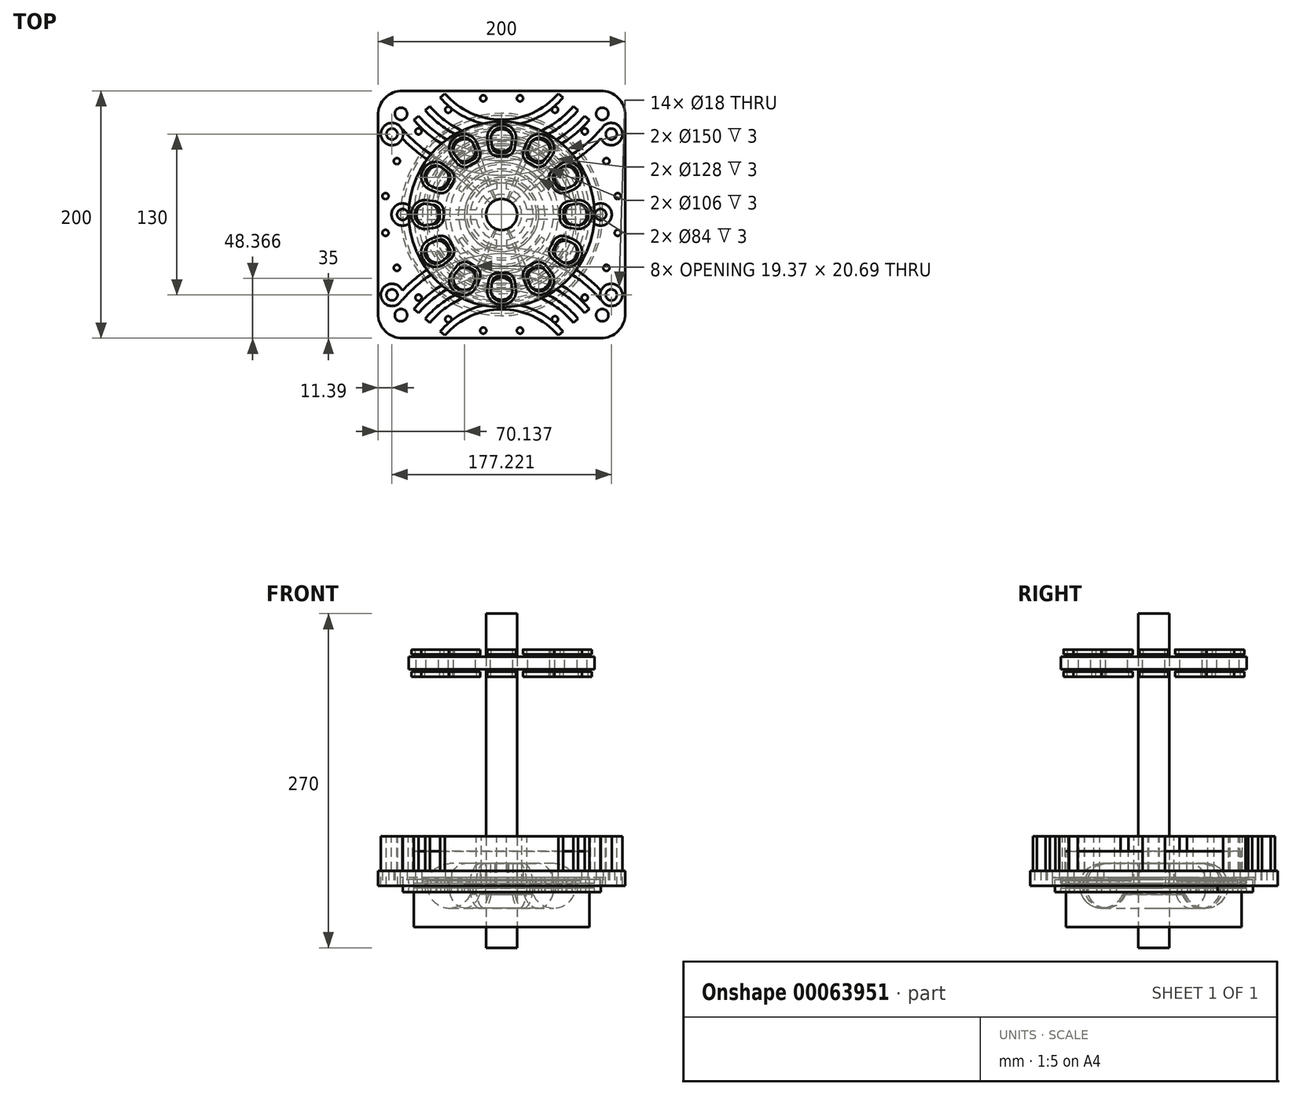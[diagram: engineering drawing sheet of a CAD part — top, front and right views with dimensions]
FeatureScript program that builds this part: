
annotation { "Feature Type Name" : "Feature", "Feature Type Description" : "" }
export const myFeature = defineFeature(function(context is Context, id is Id, definition is map)
    precondition{}
    {
        {
            var Q0;
            Q0=qCreatedBy(makeId("Top.planeOp"),FACE);
            var sketch = newSketch(context, id + "F0", { "sketchPlane" : qUnion([Q0])});
            skCircle(sketch, "E0", {"center": v(0, 0) * mm, "radius": 80 * mm});
            skCircle(sketch, "E1", {"center": v(0, 0) * mm, "radius": 30 * mm});
            skLineSegment(sketch, "E2", {"start": v(0, 30) * mm, "end": v(0, 80) * mm});
            skCircle(sketch, "E3", {"center": v(0, 0) * mm, "radius": 12.5 * mm});
            skLineSegment(sketch, "E4", {"start": v(0, 30) * mm, "end": v(0, 12.5) * mm});
            skLineSegment(sketch, "E5", {"start": v(-61.28, 51.42) * mm, "end": v(-22.98, 19.28) * mm});
            skLineSegment(sketch, "E6", {"start": v(0, 80) * mm, "end": v(0, 109.43) * mm, "construction": true});
            skLineSegment(sketch, "E7.MirrorCS", {"start": v(61.28, 51.42) * mm, "end": v(22.98, 19.28) * mm});
            skLineSegment(sketch, "E8", {"start": v(80, 0) * mm, "end": v(100, 0) * mm});
            skLineSegment(sketch, "E9", {"start": v(100, 0) * mm, "end": v(100, 80) * mm});
            skLineSegment(sketch, "E10", {"start": v(80, 100) * mm, "end": v(0, 100) * mm});
            skLineSegment(sketch, "E11", {"start": v(0, 100) * mm, "end": v(0, 80) * mm});
            skCircle(sketch, "E12", {"center": v(0, 0) * mm, "radius": 90 * mm});
            skLineSegment(sketch, "E13", {"start": v(0, 0) * mm, "end": v(0, -92.84) * mm, "construction": true});
            skLineSegment(sketch, "E14", {"start": v(0, 0) * mm, "end": v(-115.3, 0) * mm, "construction": true});
            skPoint(sketch, "E15", {"position": v(0, 90) * mm});
            skCircle(sketch, "E16", {"center": v(0, 0) * mm, "radius": 95 * mm, "construction": true});
            skCircle(sketch, "E17", {"center": v(67.18, 67.18) * mm, "radius": 2.5 * mm});
            skCircle(sketch, "E18", {"center": v(84.65, 43.13) * mm, "radius": 2.5 * mm});
            skCircle(sketch, "E19", {"center": v(93.83, 14.86) * mm, "radius": 2.5 * mm});
            skCircle(sketch, "E20", {"center": v(43.13, 84.65) * mm, "radius": 2.5 * mm});
            skCircle(sketch, "E21", {"center": v(14.86, 93.83) * mm, "radius": 2.5 * mm});
            skLineSegment(sketch, "E22", {"start": v(0, 0) * mm, "end": v(67.18, 67.18) * mm, "construction": true});
            skLineSegment(sketch, "E23", {"start": v(43.13, 84.65) * mm, "end": v(0, 0) * mm, "construction": true});
            skLineSegment(sketch, "E24", {"start": v(14.86, 93.83) * mm, "end": v(0, 0) * mm, "construction": true});
            skLineSegment(sketch, "E25", {"start": v(84.65, 43.13) * mm, "end": v(0, 0) * mm, "construction": true});
            skLineSegment(sketch, "E26", {"start": v(93.83, 14.86) * mm, "end": v(0, 0) * mm, "construction": true});
            skCircle(sketch, "E27", {"center": v(81.32, 81.32) * mm, "radius": 5 * mm});
            skLineSegment(sketch, "E28", {"start": v(67.18, 67.18) * mm, "end": v(81.32, 81.32) * mm, "construction": true});
            skCircle(sketch, "E29", {"center": v(0, 0) * mm, "radius": 115 * mm, "construction": true});
            skPoint(sketch, "E30.visualSharp", {"position": v(100, 100) * mm});
            skArc(sketch, "E30.filletArc", {"start": v(100, 80) * mm, "mid": v(94.14, 94.14) * mm, "end": v(80, 100) * mm});
            skSolve(sketch);
        }
        {
            var Q0;
            Q0=qCreatedBy(makeId("Right.planeOp"),FACE);
            var sketch = newSketch(context, id + "F1", { "sketchPlane" : qUnion([Q0])});
            skLineSegment(sketch, "E31.rect.bottom", {"start": v(80, -5) * mm, "end": v(75, -5) * mm});
            skLineSegment(sketch, "E31.rect.top", {"start": v(80, 5) * mm, "end": v(75, 5) * mm});
            skLineSegment(sketch, "E31.rect.left", {"start": v(80, -5) * mm, "end": v(80, 5) * mm});
            skLineSegment(sketch, "E31.rect.right", {"start": v(30, -5) * mm, "end": v(30, 5) * mm});
            skPoint(sketch, "E31.rect.middle", {"position": v(55, 0) * mm});
            skLineSegment(sketch, "E32.rect.bottom", {"start": v(30, -2) * mm, "end": v(12.5, -2) * mm});
            skLineSegment(sketch, "E32.rect.top", {"start": v(30, 2) * mm, "end": v(12.5, 2) * mm});
            skLineSegment(sketch, "E32.rect.left", {"start": v(30, -2) * mm, "end": v(30, 2) * mm});
            skLineSegment(sketch, "E32.rect.right", {"start": v(12.5, -2) * mm, "end": v(12.5, 2) * mm});
            skPoint(sketch, "E32.rect.middle", {"position": v(21.25, 0) * mm});
            skLineSegment(sketch, "E33", {"start": v(0, -7.1) * mm, "end": v(0, -52.53) * mm});
            skLineSegment(sketch, "E34", {"start": v(35, 5) * mm, "end": v(35, 2) * mm});
            skLineSegment(sketch, "E35", {"start": v(35, 2) * mm, "end": v(42, 2) * mm});
            skLineSegment(sketch, "E36", {"start": v(42, 2) * mm, "end": v(42, 5) * mm});
            skLineSegment(sketch, "E37.top", {"start": v(46, 2) * mm, "end": v(53, 2) * mm});
            skLineSegment(sketch, "E37.left", {"start": v(46, 5) * mm, "end": v(46, 2) * mm});
            skLineSegment(sketch, "E37.right", {"start": v(53, 5) * mm, "end": v(53, 2) * mm});
            skLineSegment(sketch, "E38.top", {"start": v(57, 2) * mm, "end": v(64, 2) * mm});
            skLineSegment(sketch, "E38.left", {"start": v(57, 5) * mm, "end": v(57, 2) * mm});
            skLineSegment(sketch, "E38.right", {"start": v(64, 5) * mm, "end": v(64, 2) * mm});
            skLineSegment(sketch, "E39.top", {"start": v(68, 2) * mm, "end": v(75, 2) * mm});
            skLineSegment(sketch, "E39.left", {"start": v(68, 5) * mm, "end": v(68, 2) * mm});
            skLineSegment(sketch, "E39.right", {"start": v(75, 5) * mm, "end": v(75, 2) * mm});
            skPoint(sketch, "E40", {"position": v(38.5, 2) * mm});
            skPoint(sketch, "E41", {"position": v(49.5, 2) * mm});
            skPoint(sketch, "E42", {"position": v(60.5, 2) * mm});
            skPoint(sketch, "E43", {"position": v(71.5, 2) * mm});
            skLineSegment(sketch, "E44.MirrorCS", {"start": v(75, -5) * mm, "end": v(75, -2) * mm});
            skLineSegment(sketch, "E45.MirrorCS", {"start": v(68, -2) * mm, "end": v(75, -2) * mm});
            skLineSegment(sketch, "E46.MirrorCS", {"start": v(68, -5) * mm, "end": v(68, -2) * mm});
            skLineSegment(sketch, "E47.MirrorCS", {"start": v(64, -5) * mm, "end": v(64, -2) * mm});
            skLineSegment(sketch, "E48.MirrorCS", {"start": v(57, -2) * mm, "end": v(64, -2) * mm});
            skLineSegment(sketch, "E49.MirrorCS", {"start": v(57, -5) * mm, "end": v(57, -2) * mm});
            skLineSegment(sketch, "E50.MirrorCS", {"start": v(53, -5) * mm, "end": v(53, -2) * mm});
            skLineSegment(sketch, "E51.MirrorCS", {"start": v(46, -2) * mm, "end": v(53, -2) * mm});
            skLineSegment(sketch, "E52.MirrorCS", {"start": v(46, -5) * mm, "end": v(46, -2) * mm});
            skLineSegment(sketch, "E53.MirrorCS", {"start": v(42, -2) * mm, "end": v(42, -5) * mm});
            skLineSegment(sketch, "E54.MirrorCS", {"start": v(35, -2) * mm, "end": v(42, -2) * mm});
            skLineSegment(sketch, "E55.MirrorCS", {"start": v(35, -5) * mm, "end": v(35, -2) * mm});
            skLineSegment(sketch, "E56.trimOffspring", {"start": v(35, 5) * mm, "end": v(30, 5) * mm});
            skLineSegment(sketch, "E57.trimOffspring", {"start": v(46, 5) * mm, "end": v(42, 5) * mm});
            skLineSegment(sketch, "E58.trimOffspring", {"start": v(57, 5) * mm, "end": v(53, 5) * mm});
            skLineSegment(sketch, "E59.trimOffspring", {"start": v(68, 5) * mm, "end": v(64, 5) * mm});
            skLineSegment(sketch, "E60.trimOffspring", {"start": v(68, -5) * mm, "end": v(64, -5) * mm});
            skLineSegment(sketch, "E61.trimOffspring", {"start": v(57, -5) * mm, "end": v(53, -5) * mm});
            skLineSegment(sketch, "E62.trimOffspring", {"start": v(46, -5) * mm, "end": v(42, -5) * mm});
            skLineSegment(sketch, "E63.trimOffspring", {"start": v(35, -5) * mm, "end": v(30, -5) * mm});
            skLineSegment(sketch, "E64.0", {"start": v(36.75, 6.75) * mm, "end": v(28.25, 6.75) * mm});
            skLineSegment(sketch, "E64.1", {"start": v(28.25, -6.75) * mm, "end": v(28.25, 6.75) * mm});
            skLineSegment(sketch, "E64.2", {"start": v(36.75, -6.75) * mm, "end": v(28.25, -6.75) * mm});
            skLineSegment(sketch, "E64.3", {"start": v(36.75, -6.75) * mm, "end": v(36.75, -3.75) * mm});
            skLineSegment(sketch, "E64.4", {"start": v(36.75, -3.75) * mm, "end": v(40.25, -3.75) * mm});
            skLineSegment(sketch, "E64.5", {"start": v(40.25, -3.75) * mm, "end": v(40.25, -6.75) * mm});
            skLineSegment(sketch, "E64.6", {"start": v(47.75, -6.75) * mm, "end": v(40.25, -6.75) * mm});
            skLineSegment(sketch, "E64.7", {"start": v(47.75, -6.75) * mm, "end": v(47.75, -3.75) * mm});
            skLineSegment(sketch, "E64.8", {"start": v(47.75, -3.75) * mm, "end": v(51.25, -3.75) * mm});
            skLineSegment(sketch, "E64.9", {"start": v(51.25, -6.75) * mm, "end": v(51.25, -3.75) * mm});
            skLineSegment(sketch, "E64.10", {"start": v(58.75, -6.75) * mm, "end": v(51.25, -6.75) * mm});
            skLineSegment(sketch, "E64.11", {"start": v(36.75, 6.75) * mm, "end": v(36.75, 3.75) * mm});
            skLineSegment(sketch, "E64.12", {"start": v(58.75, -6.75) * mm, "end": v(58.75, -3.75) * mm});
            skLineSegment(sketch, "E64.13", {"start": v(58.75, -3.75) * mm, "end": v(62.25, -3.75) * mm});
            skLineSegment(sketch, "E64.14", {"start": v(62.25, 6.75) * mm, "end": v(62.25, 3.75) * mm});
            skLineSegment(sketch, "E64.15", {"start": v(58.75, 3.75) * mm, "end": v(62.25, 3.75) * mm});
            skLineSegment(sketch, "E64.16", {"start": v(58.75, 6.75) * mm, "end": v(58.75, 3.75) * mm});
            skLineSegment(sketch, "E64.17", {"start": v(58.75, 6.75) * mm, "end": v(51.25, 6.75) * mm});
            skLineSegment(sketch, "E64.18", {"start": v(51.25, 6.75) * mm, "end": v(51.25, 3.75) * mm});
            skLineSegment(sketch, "E64.19", {"start": v(47.75, 3.75) * mm, "end": v(51.25, 3.75) * mm});
            skLineSegment(sketch, "E64.20", {"start": v(36.75, 3.75) * mm, "end": v(40.25, 3.75) * mm});
            skLineSegment(sketch, "E64.21", {"start": v(40.25, 3.75) * mm, "end": v(40.25, 6.75) * mm});
            skLineSegment(sketch, "E64.22", {"start": v(47.75, 6.75) * mm, "end": v(40.25, 6.75) * mm});
            skLineSegment(sketch, "E64.23", {"start": v(47.75, 6.75) * mm, "end": v(47.75, 3.75) * mm});
            skLineSegment(sketch, "E64.24", {"start": v(69.75, 6.75) * mm, "end": v(62.25, 6.75) * mm});
            skLineSegment(sketch, "E64.25", {"start": v(69.75, 6.75) * mm, "end": v(69.75, 3.75) * mm});
            skLineSegment(sketch, "E64.26", {"start": v(69.75, 3.75) * mm, "end": v(73.25, 3.75) * mm});
            skLineSegment(sketch, "E64.27", {"start": v(73.25, 6.75) * mm, "end": v(73.25, 3.75) * mm});
            skLineSegment(sketch, "E64.28", {"start": v(81.75, 6.75) * mm, "end": v(73.25, 6.75) * mm});
            skLineSegment(sketch, "E64.29", {"start": v(81.75, -6.75) * mm, "end": v(81.75, 6.75) * mm});
            skLineSegment(sketch, "E64.30", {"start": v(81.75, -6.75) * mm, "end": v(73.25, -6.75) * mm});
            skLineSegment(sketch, "E64.31", {"start": v(73.25, -6.75) * mm, "end": v(73.25, -3.75) * mm});
            skLineSegment(sketch, "E64.32", {"start": v(69.75, -3.75) * mm, "end": v(73.25, -3.75) * mm});
            skLineSegment(sketch, "E64.33", {"start": v(69.75, -6.75) * mm, "end": v(69.75, -3.75) * mm});
            skLineSegment(sketch, "E64.34", {"start": v(69.75, -6.75) * mm, "end": v(62.25, -6.75) * mm});
            skLineSegment(sketch, "E64.35", {"start": v(62.25, -6.75) * mm, "end": v(62.25, -3.75) * mm});
            skLineSegment(sketch, "E65.bottom", {"start": v(90, 0) * mm, "end": v(16.2, 0) * mm});
            skLineSegment(sketch, "E65.top", {"start": v(90, 12) * mm, "end": v(16.2, 12) * mm});
            skLineSegment(sketch, "E65.left", {"start": v(90, 0) * mm, "end": v(90, 12) * mm});
            skLineSegment(sketch, "E65.right", {"start": v(16.2, 0) * mm, "end": v(16.2, 12) * mm});
            skLineSegment(sketch, "E66.MirrorCS", {"start": v(90, 0) * mm, "end": v(90, -12) * mm});
            skLineSegment(sketch, "E67.MirrorCS", {"start": v(90, -12) * mm, "end": v(16.2, -12) * mm});
            skLineSegment(sketch, "E68.MirrorCS", {"start": v(16.2, 0) * mm, "end": v(16.2, -12) * mm});
            skSolve(sketch);
        }
        {
            var Q0;
            {var subQ0=sQuery(id+"F1.wireOp",EDGE,"E31.rect.top");Q0=makeQuery(id+"F1.imprint","IMPRINT",FACE,{"disambiguationData":[TD([[makeQuery(id+"F1.imprint","IMPRINT",EDGE,{"derivedFrom":subQ0}),1.0]])]});}
            var Q1;
            {var subQ1=sQuery(id+"F1.wireOp",EDGE,"E31.rect.bottom");Q1=makeQuery(id+"F1.imprint","IMPRINT",FACE,{"disambiguationData":[TD([[makeQuery(id+"F1.imprint","IMPRINT",EDGE,{"derivedFrom":subQ1}),-1.0]])]});}
            var Q2;
            Q2=sQuery(id+"F1.wireOp",EDGE,"E33");
            revolve(context, id + "F2", {"entities" : qUnion([Q0, Q1]), "axis" : qUnion([Q2]), "revolveType" : RevolveType.SYMMETRIC, "angle" : 100 * degree});
        }
        {
            var Q0;
            {var subQ5=sQuery(id+"F1.wireOp",EDGE,"E32.rect.right");Q0=makeQuery(id+"F1.imprint","IMPRINT",FACE,{"disambiguationData":[TD([[makeQuery(id+"F1.imprint","IMPRINT",EDGE,{"derivedFrom":subQ5}),-1.0]])]});}
            var Q1;
            {var subQ0=sQuery(id+"F1.wireOp",EDGE,"E65.right");var subQ1=sQuery(id+"F1.wireOp",EDGE,"E32.rect.top");var subQ2=makeQuery(id+"F1.imprint","INTERSECT",VERTEX,{"derivedFrom":[subQ1,subQ0]});Q1=makeQuery(id+"F1.imprint","IMPRINT",FACE,{"disambiguationData":[TD([[makeQuery(id+"F1.imprint","IMPRINT",EDGE,{"disambiguationData":[TD([[subQ2,1.0]])],"derivedFrom":subQ1}),1.0]])]});}
            var Q2;
            {var subQ1=sQuery(id+"F1.wireOp",EDGE,"E32.rect.top");var subQ3=sQuery(id+"F1.wireOp",EDGE,"E64.1");var subQ4=makeQuery(id+"F1.imprint","INTERSECT",VERTEX,{"derivedFrom":[subQ1,subQ3]});Q2=makeQuery(id+"F1.imprint","IMPRINT",FACE,{"disambiguationData":[TD([[makeQuery(id+"F1.imprint","IMPRINT",EDGE,{"disambiguationData":[TD([[subQ4,1.0]])],"derivedFrom":subQ3}),-1.0]])]});}
            var Q3;
            {var subQ1=sQuery(id+"F1.wireOp",EDGE,"E32.rect.bottom");var subQ3=sQuery(id+"F1.wireOp",EDGE,"E64.1");var subQ4=makeQuery(id+"F1.imprint","INTERSECT",VERTEX,{"derivedFrom":[subQ1,subQ3]});Q3=makeQuery(id+"F1.imprint","IMPRINT",FACE,{"disambiguationData":[TD([[makeQuery(id+"F1.imprint","IMPRINT",EDGE,{"disambiguationData":[TD([[subQ4,-1.0]])],"derivedFrom":subQ3}),-1.0]])]});}
            var Q4;
            {var subQ0=sQuery(id+"F1.wireOp",EDGE,"E68.MirrorCS");var subQ1=sQuery(id+"F1.wireOp",EDGE,"E32.rect.bottom");var subQ2=makeQuery(id+"F1.imprint","INTERSECT",VERTEX,{"derivedFrom":[subQ1,subQ0]});Q4=makeQuery(id+"F1.imprint","IMPRINT",FACE,{"disambiguationData":[TD([[makeQuery(id+"F1.imprint","IMPRINT",EDGE,{"disambiguationData":[TD([[subQ2,1.0]])],"derivedFrom":subQ1}),-1.0]])]});}
            var Q5;
            Q5=makeQuery(id+"F2.opRevolve","SWEPT_FACE",FACE,{"disambiguationData":[OSD([sQuery(id+"F1.wireOp",EDGE,"E31.rect.left")])]});
            revolve(context, id + "F3", {"operationType" : NewBodyOperationType.ADD, "entities" : qUnion([Q0, Q1, Q2, Q3, Q4]), "axis" : qUnion([Q5]), "revolveType" : RevolveType.FULL});
        }
        {
            var Q0;
            {var subQ7=sQuery(id+"F1.wireOp",EDGE,"E64.0");Q0=makeQuery(id+"F1.imprint","IMPRINT",FACE,{"disambiguationData":[TD([[makeQuery(id+"F1.imprint","IMPRINT",EDGE,{"derivedFrom":subQ7}),-1.0]])]});}
            var Q1;
            Q1=sQuery(id+"F1.wireOp",EDGE,"E33");
            revolve(context, id + "F4", {"entities" : qUnion([Q0]), "axis" : qUnion([Q1]), "revolveType" : RevolveType.FULL});
        }
        {
            var Q0;
            {var subQ5=sQuery(id+"F0.wireOp",EDGE,"E9");Q0=makeQuery(id+"F0.imprint","IMPRINT",FACE,{"disambiguationData":[TD([[makeQuery(id+"F0.imprint","IMPRINT",EDGE,{"derivedFrom":subQ5}),1.0]])]});}
            extrude(context, id + "F5", {"entities" : qUnion([Q0]), "depth" : 12 * mm});
        }
        {
            var Q0;
            Q0=makeQuery(id+"F5.opExtrude","SWEPT_BODY",BODY,{"disambiguationData":[OSD([sQuery(id+"F0.wireOp",EDGE,"E8"),sQuery(id+"F0.wireOp",EDGE,"E9"),sQuery(id+"F0.wireOp",EDGE,"E10"),sQuery(id+"F0.wireOp",EDGE,"E11"),sQuery(id+"F0.wireOp",EDGE,"E12"),sQuery(id+"F0.wireOp",EDGE,"E17"),sQuery(id+"F0.wireOp",EDGE,"E18"),sQuery(id+"F0.wireOp",EDGE,"E19"),sQuery(id+"F0.wireOp",EDGE,"E20"),sQuery(id+"F0.wireOp",EDGE,"E21"),sQuery(id+"F0.wireOp",EDGE,"E27"),sQuery(id+"F0.wireOp",EDGE,"E30.filletArc")])]});
            var Q1;
            Q1=qCreatedBy(makeId("Front.planeOp"),FACE);
            mirror(context, id + "F6", {"entities" : qUnion([Q0]), "mirrorPlane" : qUnion([Q1])});
        }
        {
            var Q0;
            Q0=makeQuery(id+"F5.opExtrude","SWEPT_BODY",BODY,{"disambiguationData":[OSD([sQuery(id+"F0.wireOp",EDGE,"E8"),sQuery(id+"F0.wireOp",EDGE,"E9"),sQuery(id+"F0.wireOp",EDGE,"E10"),sQuery(id+"F0.wireOp",EDGE,"E11"),sQuery(id+"F0.wireOp",EDGE,"E12"),sQuery(id+"F0.wireOp",EDGE,"E17"),sQuery(id+"F0.wireOp",EDGE,"E18"),sQuery(id+"F0.wireOp",EDGE,"E19"),sQuery(id+"F0.wireOp",EDGE,"E20"),sQuery(id+"F0.wireOp",EDGE,"E21"),sQuery(id+"F0.wireOp",EDGE,"E27"),sQuery(id+"F0.wireOp",EDGE,"E30.filletArc")])]});
            var Q1;
            Q1=makeQuery(id+"F6.opPattern","COPY",BODY,{"derivedFrom":makeQuery(id+"F5.opExtrude","SWEPT_BODY",BODY,{"disambiguationData":[OSD([sQuery(id+"F0.wireOp",EDGE,"E8"),sQuery(id+"F0.wireOp",EDGE,"E9"),sQuery(id+"F0.wireOp",EDGE,"E10"),sQuery(id+"F0.wireOp",EDGE,"E11"),sQuery(id+"F0.wireOp",EDGE,"E12"),sQuery(id+"F0.wireOp",EDGE,"E17"),sQuery(id+"F0.wireOp",EDGE,"E18"),sQuery(id+"F0.wireOp",EDGE,"E19"),sQuery(id+"F0.wireOp",EDGE,"E20"),sQuery(id+"F0.wireOp",EDGE,"E21"),sQuery(id+"F0.wireOp",EDGE,"E27"),sQuery(id+"F0.wireOp",EDGE,"E30.filletArc")])]}),"instanceName":"1"});
            var Q2;
            Q2=qCreatedBy(makeId("Right.planeOp"),FACE);
            mirror(context, id + "F7", {"entities" : qUnion([Q0, Q1]), "mirrorPlane" : qUnion([Q2])});
        }
        {
            var Q0;
            Q0=makeQuery(id+"F5.opExtrude","SWEPT_BODY",BODY,{"disambiguationData":[OSD([sQuery(id+"F0.wireOp",EDGE,"E8"),sQuery(id+"F0.wireOp",EDGE,"E9"),sQuery(id+"F0.wireOp",EDGE,"E10"),sQuery(id+"F0.wireOp",EDGE,"E11"),sQuery(id+"F0.wireOp",EDGE,"E12"),sQuery(id+"F0.wireOp",EDGE,"E17"),sQuery(id+"F0.wireOp",EDGE,"E18"),sQuery(id+"F0.wireOp",EDGE,"E19"),sQuery(id+"F0.wireOp",EDGE,"E20"),sQuery(id+"F0.wireOp",EDGE,"E21"),sQuery(id+"F0.wireOp",EDGE,"E27"),sQuery(id+"F0.wireOp",EDGE,"E30.filletArc")])]});
            var Q1;
            Q1=makeQuery(id+"F7.opPattern","COPY",BODY,{"derivedFrom":makeQuery(id+"F5.opExtrude","SWEPT_BODY",BODY,{"disambiguationData":[OSD([sQuery(id+"F0.wireOp",EDGE,"E8"),sQuery(id+"F0.wireOp",EDGE,"E9"),sQuery(id+"F0.wireOp",EDGE,"E10"),sQuery(id+"F0.wireOp",EDGE,"E11"),sQuery(id+"F0.wireOp",EDGE,"E12"),sQuery(id+"F0.wireOp",EDGE,"E17"),sQuery(id+"F0.wireOp",EDGE,"E18"),sQuery(id+"F0.wireOp",EDGE,"E19"),sQuery(id+"F0.wireOp",EDGE,"E20"),sQuery(id+"F0.wireOp",EDGE,"E21"),sQuery(id+"F0.wireOp",EDGE,"E27"),sQuery(id+"F0.wireOp",EDGE,"E30.filletArc")])]}),"instanceName":"1"});
            var Q2;
            Q2=makeQuery(id+"F7.opPattern","COPY",BODY,{"derivedFrom":makeQuery(id+"F6.opPattern","COPY",BODY,{"derivedFrom":makeQuery(id+"F5.opExtrude","SWEPT_BODY",BODY,{"disambiguationData":[OSD([sQuery(id+"F0.wireOp",EDGE,"E8"),sQuery(id+"F0.wireOp",EDGE,"E9"),sQuery(id+"F0.wireOp",EDGE,"E10"),sQuery(id+"F0.wireOp",EDGE,"E11"),sQuery(id+"F0.wireOp",EDGE,"E12"),sQuery(id+"F0.wireOp",EDGE,"E17"),sQuery(id+"F0.wireOp",EDGE,"E18"),sQuery(id+"F0.wireOp",EDGE,"E19"),sQuery(id+"F0.wireOp",EDGE,"E20"),sQuery(id+"F0.wireOp",EDGE,"E21"),sQuery(id+"F0.wireOp",EDGE,"E27"),sQuery(id+"F0.wireOp",EDGE,"E30.filletArc")])]}),"instanceName":"1"}),"instanceName":"1"});
            var Q3;
            Q3=makeQuery(id+"F6.opPattern","COPY",BODY,{"derivedFrom":makeQuery(id+"F5.opExtrude","SWEPT_BODY",BODY,{"disambiguationData":[OSD([sQuery(id+"F0.wireOp",EDGE,"E8"),sQuery(id+"F0.wireOp",EDGE,"E9"),sQuery(id+"F0.wireOp",EDGE,"E10"),sQuery(id+"F0.wireOp",EDGE,"E11"),sQuery(id+"F0.wireOp",EDGE,"E12"),sQuery(id+"F0.wireOp",EDGE,"E17"),sQuery(id+"F0.wireOp",EDGE,"E18"),sQuery(id+"F0.wireOp",EDGE,"E19"),sQuery(id+"F0.wireOp",EDGE,"E20"),sQuery(id+"F0.wireOp",EDGE,"E21"),sQuery(id+"F0.wireOp",EDGE,"E27"),sQuery(id+"F0.wireOp",EDGE,"E30.filletArc")])]}),"instanceName":"1"});
            booleanBodies(context, id + "F8", {"operationType" : BooleanOperationType.UNION, "tools" : qUnion([Q0, Q1, Q2, Q3])});
        }
        {
            var Q0;
            Q0=qCreatedBy(makeId("Top.planeOp"),FACE);
            var sketch = newSketch(context, id + "F9", { "sketchPlane" : qUnion([Q0])});
            skLineSegment(sketch, "E69", {"start": v(0, 0) * mm, "end": v(-124.58, 0) * mm, "construction": true});
            skLineSegment(sketch, "E70", {"start": v(25.98, -15) * mm, "end": v(64.95, -37.5) * mm});
            skArc(sketch, "E71", {"start": v(64.95, -37.5) * mm, "mid": v(75, 0) * mm, "end": v(64.95, 37.5) * mm});
            skArc(sketch, "E72", {"start": v(25.98, -15) * mm, "mid": v(30, 0) * mm, "end": v(25.98, 15) * mm});
            skLineSegment(sketch, "E73", {"start": v(-25.98, -15) * mm, "end": v(-64.95, -37.5) * mm});
            skLineSegment(sketch, "E74.MirrorCS", {"start": v(-25.98, 15) * mm, "end": v(-64.95, 37.5) * mm});
            skLineSegment(sketch, "E75.MirrorCS", {"start": v(25.98, 15) * mm, "end": v(64.95, 37.5) * mm});
            skArc(sketch, "E76.trimOffspring", {"start": v(-25.98, 15) * mm, "mid": v(-30, 0) * mm, "end": v(-25.98, -15) * mm});
            skArc(sketch, "E77.trimOffspring", {"start": v(-64.95, 37.5) * mm, "mid": v(-75, 0) * mm, "end": v(-64.95, -37.5) * mm});
            skSolve(sketch);
        }
        {
            var Q0;
            Q0=makeQuery(id+"F9.imprint","IMPRINT",FACE,{"disambiguationData":[TD([[makeQuery(id+"F9.imprint","IMPRINT",EDGE,{"derivedFrom":sQuery(id+"F9.wireOp",EDGE,"E73")}),-1.0]])]});
            var Q1;
            Q1=makeQuery(id+"F9.imprint","IMPRINT",FACE,{"disambiguationData":[TD([[makeQuery(id+"F9.imprint","IMPRINT",EDGE,{"derivedFrom":sQuery(id+"F9.wireOp",EDGE,"E70")}),1.0]])]});
            var Q2;
            Q2=makeQuery(id+"F4.opRevolve","SWEPT_FACE",FACE,{"disambiguationData":[OSD([sQuery(id+"F1.wireOp",EDGE,"E64.24")])]});
            extrude(context, id + "F10", {"entities" : qUnion([Q0, Q1]), "operationType" : NewBodyOperationType.REMOVE, "endBound" : BoundingType.UP_TO_SURFACE, "endBoundEntityFace" : qUnion([Q2]), "depth" : 25 * mm});
        }
        {
            var Q0;
            Q0=makeQuery(id+"F4.opRevolve","SWEPT_BODY",BODY,{"disambiguationData":[OSD([sQuery(id+"F1.wireOp",EDGE,"E32.rect.top"),sQuery(id+"F1.wireOp",EDGE,"E64.0"),sQuery(id+"F1.wireOp",EDGE,"E64.1"),sQuery(id+"F1.wireOp",EDGE,"E64.11"),sQuery(id+"F1.wireOp",EDGE,"E64.14"),sQuery(id+"F1.wireOp",EDGE,"E64.15"),sQuery(id+"F1.wireOp",EDGE,"E64.16"),sQuery(id+"F1.wireOp",EDGE,"E64.17"),sQuery(id+"F1.wireOp",EDGE,"E64.18"),sQuery(id+"F1.wireOp",EDGE,"E64.19"),sQuery(id+"F1.wireOp",EDGE,"E64.20"),sQuery(id+"F1.wireOp",EDGE,"E64.21"),sQuery(id+"F1.wireOp",EDGE,"E64.22"),sQuery(id+"F1.wireOp",EDGE,"E64.23"),sQuery(id+"F1.wireOp",EDGE,"E64.24"),sQuery(id+"F1.wireOp",EDGE,"E64.25"),sQuery(id+"F1.wireOp",EDGE,"E64.26"),sQuery(id+"F1.wireOp",EDGE,"E64.27"),sQuery(id+"F1.wireOp",EDGE,"E64.28"),sQuery(id+"F1.wireOp",EDGE,"E64.29"),sQuery(id+"F1.wireOp",EDGE,"E65.bottom"),sQuery(id+"F1.wireOp",EDGE,"E65.top"),sQuery(id+"F1.wireOp",EDGE,"E65.left"),sQuery(id+"F1.wireOp",EDGE,"E65.right")])]});
            var Q1;
            Q1=makeQuery(id+"F5.opExtrude","SWEPT_BODY",BODY,{"disambiguationData":[OSD([sQuery(id+"F0.wireOp",EDGE,"E8"),sQuery(id+"F0.wireOp",EDGE,"E9"),sQuery(id+"F0.wireOp",EDGE,"E10"),sQuery(id+"F0.wireOp",EDGE,"E11"),sQuery(id+"F0.wireOp",EDGE,"E12"),sQuery(id+"F0.wireOp",EDGE,"E17"),sQuery(id+"F0.wireOp",EDGE,"E18"),sQuery(id+"F0.wireOp",EDGE,"E19"),sQuery(id+"F0.wireOp",EDGE,"E20"),sQuery(id+"F0.wireOp",EDGE,"E21"),sQuery(id+"F0.wireOp",EDGE,"E27"),sQuery(id+"F0.wireOp",EDGE,"E30.filletArc")])]});
            booleanBodies(context, id + "F11", {"operationType" : BooleanOperationType.UNION, "tools" : qUnion([Q0, Q1])});
        }
        {
            var Q0;
            Q0=qCreatedBy(makeId("Top.planeOp"),FACE);
            cPlane(context, id + "F12", {"entities" : qUnion([Q0]), "cplaneType" : CPlaneType.OFFSET, "offset" : 40 * mm, "width" : 150 * mm, "height" : 150 * mm});
        }
        {
            var Q0;
            Q0=qCreatedBy(id+"F12.planeOp",FACE);
            var sketch = newSketch(context, id + "F13", { "sketchPlane" : qUnion([Q0])});
            skArc(sketch, "E78", {"start": v(-59.84, 85.77) * mm, "mid": v(0, 58.13) * mm, "end": v(59.84, 85.77) * mm, "construction": true});
            skArc(sketch, "E79", {"start": v(-68.98, 78) * mm, "mid": v(0, 46.13) * mm, "end": v(68.98, 78) * mm, "construction": true});
            skArc(sketch, "E80", {"start": v(-81.85, 67.04) * mm, "mid": v(0, 29.22) * mm, "end": v(81.85, 67.04) * mm, "construction": true});
            skArc(sketch, "E81", {"start": v(-47.66, 96.15) * mm, "mid": v(0, 74.13) * mm, "end": v(47.66, 96.15) * mm, "construction": true});
            skLineSegment(sketch, "E82", {"start": v(0, 136.72) * mm, "end": v(-81.85, 67.04) * mm});
            skLineSegment(sketch, "E83", {"start": v(0, 0) * mm, "end": v(0, -117.9) * mm});
            skLineSegment(sketch, "E84", {"start": v(0, 0) * mm, "end": v(-143, 0) * mm});
            skLineSegment(sketch, "E85.MirrorCS", {"start": v(0, 136.72) * mm, "end": v(81.85, 67.04) * mm});
            skArc(sketch, "E86.0", {"start": v(-83.76, 65.41) * mm, "mid": v(0, 26.72) * mm, "end": v(83.76, 65.41) * mm});
            skArc(sketch, "E87.0", {"start": v(-79.95, 68.66) * mm, "mid": v(0, 31.72) * mm, "end": v(79.95, 68.66) * mm});
            skArc(sketch, "E88.0", {"start": v(-70.88, 76.37) * mm, "mid": v(0, 43.63) * mm, "end": v(70.88, 76.37) * mm});
            skArc(sketch, "E89.0", {"start": v(-67.08, 79.62) * mm, "mid": v(0, 48.63) * mm, "end": v(67.08, 79.62) * mm});
            skArc(sketch, "E90.0", {"start": v(-61.75, 84.15) * mm, "mid": v(0, 55.63) * mm, "end": v(61.75, 84.15) * mm});
            skArc(sketch, "E91.0", {"start": v(-57.94, 87.4) * mm, "mid": v(0, 60.63) * mm, "end": v(57.94, 87.4) * mm});
            skArc(sketch, "E92.0", {"start": v(-49.56, 94.53) * mm, "mid": v(0, 71.63) * mm, "end": v(49.56, 94.53) * mm});
            skArc(sketch, "E93.0", {"start": v(-45.76, 97.77) * mm, "mid": v(0, 76.63) * mm, "end": v(45.76, 97.77) * mm});
            skLineSegment(sketch, "E94", {"start": v(-81.85, 67.04) * mm, "end": v(-83.76, 65.41) * mm});
            skLineSegment(sketch, "E95", {"start": v(81.85, 67.04) * mm, "end": v(83.76, 65.41) * mm});
            skArc(sketch, "E96.MirrorCS", {"start": v(-83.76, -65.41) * mm, "mid": v(0, -26.72) * mm, "end": v(83.76, -65.41) * mm});
            skArc(sketch, "E97.MirrorCS", {"start": v(-79.95, -68.66) * mm, "mid": v(0, -31.72) * mm, "end": v(79.95, -68.66) * mm});
            skArc(sketch, "E98.MirrorCS", {"start": v(-70.88, -76.37) * mm, "mid": v(0, -43.63) * mm, "end": v(70.88, -76.37) * mm});
            skArc(sketch, "E99.MirrorCS", {"start": v(-67.08, -79.62) * mm, "mid": v(0, -48.63) * mm, "end": v(67.08, -79.62) * mm});
            skArc(sketch, "E100.MirrorCS", {"start": v(-61.75, -84.15) * mm, "mid": v(0, -55.63) * mm, "end": v(61.75, -84.15) * mm});
            skArc(sketch, "E101.MirrorCS", {"start": v(-57.94, -87.4) * mm, "mid": v(0, -60.63) * mm, "end": v(57.94, -87.4) * mm});
            skArc(sketch, "E102.MirrorCS", {"start": v(-49.56, -94.53) * mm, "mid": v(0, -71.63) * mm, "end": v(49.56, -94.53) * mm});
            skArc(sketch, "E103.MirrorCS", {"start": v(-45.76, -97.77) * mm, "mid": v(0, -76.63) * mm, "end": v(45.76, -97.77) * mm});
            skLineSegment(sketch, "E104.MirrorCS", {"start": v(0, -136.72) * mm, "end": v(-81.85, -67.04) * mm});
            skLineSegment(sketch, "E105.MirrorCS", {"start": v(0, -136.72) * mm, "end": v(81.85, -67.04) * mm});
            skLineSegment(sketch, "E106.MirrorCS", {"start": v(-81.85, -67.04) * mm, "end": v(-83.76, -65.41) * mm});
            skLineSegment(sketch, "E107.MirrorCS", {"start": v(81.85, -67.04) * mm, "end": v(83.76, -65.41) * mm});
            skSolve(sketch);
        }
        {
            var Q0;
            {var subQ0=sQuery(id+"F13.wireOp",EDGE,"E92.0");Q0=makeQuery(id+"F13.imprint","IMPRINT",FACE,{"disambiguationData":[TD([[makeQuery(id+"F13.imprint","IMPRINT",EDGE,{"derivedFrom":subQ0}),1.0]])]});}
            var Q1;
            {var subQ0=sQuery(id+"F13.wireOp",EDGE,"E90.0");Q1=makeQuery(id+"F13.imprint","IMPRINT",FACE,{"disambiguationData":[TD([[makeQuery(id+"F13.imprint","IMPRINT",EDGE,{"derivedFrom":subQ0}),1.0]])]});}
            var Q2;
            {var subQ0=sQuery(id+"F13.wireOp",EDGE,"E88.0");Q2=makeQuery(id+"F13.imprint","IMPRINT",FACE,{"disambiguationData":[TD([[makeQuery(id+"F13.imprint","IMPRINT",EDGE,{"derivedFrom":subQ0}),1.0]])]});}
            var Q3;
            Q3=makeQuery(id+"F13.imprint","IMPRINT",FACE,{"disambiguationData":[TD([[makeQuery(id+"F13.imprint","IMPRINT",EDGE,{"derivedFrom":sQuery(id+"F13.wireOp",EDGE,"E86.0")}),1.0]])]});
            var Q4;
            {var subQ5=sQuery(id+"F13.wireOp",EDGE,"E106.MirrorCS");Q4=makeQuery(id+"F13.imprint","IMPRINT",FACE,{"disambiguationData":[TD([[makeQuery(id+"F13.imprint","IMPRINT",EDGE,{"derivedFrom":subQ5}),-1.0]])]});}
            var Q5;
            {var subQ0=sQuery(id+"F13.wireOp",EDGE,"E98.MirrorCS");var subQ1=sQuery(id+"F13.wireOp",EDGE,"E83");var subQ2=makeQuery(id+"F13.imprint","INTERSECT",VERTEX,{"derivedFrom":[subQ1,subQ0]});Q5=makeQuery(id+"F13.imprint","IMPRINT",FACE,{"disambiguationData":[TD([[makeQuery(id+"F13.imprint","IMPRINT",EDGE,{"disambiguationData":[TD([[subQ2,-1.0]])],"derivedFrom":subQ1}),-1.0]])]});}
            var Q6;
            {var subQ0=sQuery(id+"F13.wireOp",EDGE,"E100.MirrorCS");var subQ1=sQuery(id+"F13.wireOp",EDGE,"E83");var subQ2=makeQuery(id+"F13.imprint","INTERSECT",VERTEX,{"derivedFrom":[subQ1,subQ0]});Q6=makeQuery(id+"F13.imprint","IMPRINT",FACE,{"disambiguationData":[TD([[makeQuery(id+"F13.imprint","IMPRINT",EDGE,{"disambiguationData":[TD([[subQ2,-1.0]])],"derivedFrom":subQ1}),-1.0]])]});}
            var Q7;
            {var subQ0=sQuery(id+"F13.wireOp",EDGE,"E103.MirrorCS");var subQ1=sQuery(id+"F13.wireOp",EDGE,"E83");var subQ2=makeQuery(id+"F13.imprint","INTERSECT",VERTEX,{"derivedFrom":[subQ1,subQ0]});Q7=makeQuery(id+"F13.imprint","IMPRINT",FACE,{"disambiguationData":[TD([[makeQuery(id+"F13.imprint","IMPRINT",EDGE,{"disambiguationData":[TD([[subQ2,1.0]])],"derivedFrom":subQ1}),-1.0]])]});}
            var Q8;
            {var subQ0=sQuery(id+"F13.wireOp",EDGE,"E103.MirrorCS");var subQ1=sQuery(id+"F13.wireOp",EDGE,"E83");var subQ2=makeQuery(id+"F13.imprint","INTERSECT",VERTEX,{"derivedFrom":[subQ1,subQ0]});Q8=makeQuery(id+"F13.imprint","IMPRINT",FACE,{"disambiguationData":[TD([[makeQuery(id+"F13.imprint","IMPRINT",EDGE,{"disambiguationData":[TD([[subQ2,1.0]])],"derivedFrom":subQ1}),1.0]])]});}
            var Q9;
            {var subQ0=sQuery(id+"F13.wireOp",EDGE,"E100.MirrorCS");var subQ1=sQuery(id+"F13.wireOp",EDGE,"E83");var subQ2=makeQuery(id+"F13.imprint","INTERSECT",VERTEX,{"derivedFrom":[subQ1,subQ0]});Q9=makeQuery(id+"F13.imprint","IMPRINT",FACE,{"disambiguationData":[TD([[makeQuery(id+"F13.imprint","IMPRINT",EDGE,{"disambiguationData":[TD([[subQ2,-1.0]])],"derivedFrom":subQ1}),1.0]])]});}
            var Q10;
            {var subQ0=sQuery(id+"F13.wireOp",EDGE,"E98.MirrorCS");var subQ1=sQuery(id+"F13.wireOp",EDGE,"E83");var subQ2=makeQuery(id+"F13.imprint","INTERSECT",VERTEX,{"derivedFrom":[subQ1,subQ0]});Q10=makeQuery(id+"F13.imprint","IMPRINT",FACE,{"disambiguationData":[TD([[makeQuery(id+"F13.imprint","IMPRINT",EDGE,{"disambiguationData":[TD([[subQ2,-1.0]])],"derivedFrom":subQ1}),1.0]])]});}
            var Q11;
            {var subQ3=sQuery(id+"F13.wireOp",EDGE,"E107.MirrorCS");Q11=makeQuery(id+"F13.imprint","IMPRINT",FACE,{"disambiguationData":[TD([[makeQuery(id+"F13.imprint","IMPRINT",EDGE,{"derivedFrom":subQ3}),1.0]])]});}
            extrude(context, id + "F14", {"entities" : qUnion([Q0, Q1, Q2, Q3, Q4, Q5, Q6, Q7, Q8, Q9, Q10, Q11]), "operationType" : NewBodyOperationType.ADD, "endBound" : BoundingType.UP_TO_NEXT, "oppositeDirection" : true, "depth" : 25 * mm});
        }
        {
            var Q0;
            Q0=qCreatedBy(id+"F12.planeOp",FACE);
            var sketch = newSketch(context, id + "F15", { "sketchPlane" : qUnion([Q0])});
            skCircle(sketch, "E108", {"center": v(0, 0) * mm, "radius": 16.2 * mm});
            skCircle(sketch, "E109", {"center": v(0, 0) * mm, "radius": 21 * mm});
            skCircle(sketch, "E110", {"center": v(80, 0) * mm, "radius": 9 * mm});
            skLineSegment(sketch, "E111", {"start": v(0, -38.6) * mm, "end": v(0, -115.51) * mm});
            skLineSegment(sketch, "E112", {"start": v(71.94, -4) * mm, "end": v(20.62, -4) * mm});
            skLineSegment(sketch, "E113", {"start": v(71.94, 4) * mm, "end": v(20.62, 4) * mm});
            skLineSegment(sketch, "E114", {"start": v(-0.94, 0) * mm, "end": v(-63.97, 0) * mm});
            skLineSegment(sketch, "E115", {"start": v(4, 20.62) * mm, "end": v(4, 28.84) * mm});
            skLineSegment(sketch, "E116", {"start": v(4, 28.84) * mm, "end": v(-4, 28.84) * mm});
            skLineSegment(sketch, "E117", {"start": v(-4, 28.84) * mm, "end": v(-4, 20.62) * mm});
            skCircle(sketch, "E118", {"center": v(80, 0) * mm, "radius": 4.5 * mm});
            skLineSegment(sketch, "E119.MirrorCS", {"start": v(-4, -28.84) * mm, "end": v(-4, -20.62) * mm});
            skLineSegment(sketch, "E120.MirrorCS", {"start": v(4, -28.84) * mm, "end": v(-4, -28.84) * mm});
            skLineSegment(sketch, "E121.MirrorCS", {"start": v(4, -20.62) * mm, "end": v(4, -28.84) * mm});
            skLineSegment(sketch, "E122.MirrorCS", {"start": v(-71.94, -4) * mm, "end": v(-20.62, -4) * mm});
            skLineSegment(sketch, "E123.MirrorCS", {"start": v(-71.94, 4) * mm, "end": v(-20.62, 4) * mm});
            skCircle(sketch, "E124.MirrorC", {"center": v(-80, 0) * mm, "radius": 9 * mm});
            skCircle(sketch, "E125.MirrorC", {"center": v(-80, 0) * mm, "radius": 4.5 * mm});
            skCircle(sketch, "E126", {"center": v(88.61, 65) * mm, "radius": 9 * mm});
            skCircle(sketch, "E127", {"center": v(88.61, 65) * mm, "radius": 4.5 * mm});
            skCircle(sketch, "E128.MirrorC", {"center": v(-88.61, 65) * mm, "radius": 9 * mm});
            skCircle(sketch, "E129.MirrorC", {"center": v(-88.61, 65) * mm, "radius": 4.5 * mm});
            skCircle(sketch, "E130.MirrorC", {"center": v(-88.61, -65) * mm, "radius": 9 * mm});
            skCircle(sketch, "E131.MirrorC", {"center": v(-88.61, -65) * mm, "radius": 4.5 * mm});
            skCircle(sketch, "E132.MirrorC", {"center": v(88.61, -65) * mm, "radius": 9 * mm});
            skCircle(sketch, "E133.MirrorC", {"center": v(88.61, -65) * mm, "radius": 4.5 * mm});
            skSolve(sketch);
        }
        {
            var Q0;
            Q0=qSketchRegion(id+"F15",true);
            var Q1;
            {var subQ0=makeQuery(id+"F5.opExtrude","CAP_FACE",FACE,{"disambiguationData":[OSD([sQuery(id+"F0.wireOp",EDGE,"E8"),sQuery(id+"F0.wireOp",EDGE,"E9"),sQuery(id+"F0.wireOp",EDGE,"E10"),sQuery(id+"F0.wireOp",EDGE,"E11"),sQuery(id+"F0.wireOp",EDGE,"E12"),sQuery(id+"F0.wireOp",EDGE,"E17"),sQuery(id+"F0.wireOp",EDGE,"E18"),sQuery(id+"F0.wireOp",EDGE,"E19"),sQuery(id+"F0.wireOp",EDGE,"E20"),sQuery(id+"F0.wireOp",EDGE,"E21"),sQuery(id+"F0.wireOp",EDGE,"E27"),sQuery(id+"F0.wireOp",EDGE,"E30.filletArc")])],"isStart":false});var subQ1=makeQuery(id+"F6.opPattern","COPY",FACE,{"derivedFrom":subQ0,"instanceName":"1"});Q1=makeQuery(id+"F11.opBoolean","MERGE",FACE,{"derivedFrom":[makeQuery(id+"F4.opRevolve","SWEPT_FACE",FACE,{"disambiguationData":[OSD([sQuery(id+"F1.wireOp",EDGE,"E65.top")])]}),makeQuery(id+"F8.opBoolean","MERGE",FACE,{"derivedFrom":[subQ0,subQ1,makeQuery(id+"F7.opPattern","COPY",FACE,{"derivedFrom":subQ0,"instanceName":"1"}),makeQuery(id+"F7.opPattern","COPY",FACE,{"derivedFrom":subQ1,"instanceName":"1"})]})]});}
            extrude(context, id + "F16", {"entities" : qUnion([Q0]), "operationType" : NewBodyOperationType.ADD, "endBound" : BoundingType.UP_TO_SURFACE, "oppositeDirection" : true, "endBoundEntityFace" : qUnion([Q1]), "depth" : 25 * mm});
        }
        {
            var Q0;
            Q0=makeQuery(id+"F15.imprint","IMPRINT",FACE,{"disambiguationData":[TD([[makeQuery(id+"F15.imprint","IMPRINT",EDGE,{"derivedFrom":sQuery(id+"F15.wireOp",EDGE,"E127")}),1.0]])]});
            var Q1;
            Q1=makeQuery(id+"F15.imprint","IMPRINT",FACE,{"disambiguationData":[TD([[makeQuery(id+"F15.imprint","IMPRINT",EDGE,{"derivedFrom":sQuery(id+"F15.wireOp",EDGE,"E129.MirrorC")}),-1.0]])]});
            var Q2;
            Q2=makeQuery(id+"F15.imprint","IMPRINT",FACE,{"disambiguationData":[TD([[makeQuery(id+"F15.imprint","IMPRINT",EDGE,{"derivedFrom":sQuery(id+"F15.wireOp",EDGE,"E131.MirrorC")}),1.0]])]});
            var Q3;
            Q3=makeQuery(id+"F15.imprint","IMPRINT",FACE,{"disambiguationData":[TD([[makeQuery(id+"F15.imprint","IMPRINT",EDGE,{"derivedFrom":sQuery(id+"F15.wireOp",EDGE,"E133.MirrorC")}),-1.0]])]});
            extrude(context, id + "F17", {"entities" : qUnion([Q0, Q1, Q2, Q3]), "operationType" : NewBodyOperationType.REMOVE, "oppositeDirection" : true, "depth" : 50 * mm});
        }
        {
            var Q0;
            Q0=qCreatedBy(makeId("Top.planeOp"),FACE);
            cPlane(context, id + "F18", {"entities" : qUnion([Q0]), "cplaneType" : CPlaneType.OFFSET, "offset" : 180 * mm, "width" : 150 * mm, "height" : 150 * mm});
        }
        {
            var Q0;
            Q0=qCreatedBy(id+"F18.planeOp",FACE);
            var sketch = newSketch(context, id + "F19", { "sketchPlane" : qUnion([Q0])});
            skCircle(sketch, "E134", {"center": v(0, 0) * mm, "radius": 12.5 * mm});
            skCircle(sketch, "E135", {"center": v(0, 0) * mm, "radius": 75 * mm});
            skSolve(sketch);
        }
        {
            var Q0;
            Q0=makeQuery(id+"F19.imprint","IMPRINT",FACE,{"disambiguationData":[TD([[makeQuery(id+"F19.imprint","IMPRINT",EDGE,{"derivedFrom":sQuery(id+"F19.wireOp",EDGE,"E134")}),-1.0]])]});
            extrude(context, id + "F20", {"entities" : qUnion([Q0]), "endBound" : BoundingType.SYMMETRIC, "depth" : 10 * mm});
        }
        {
            var Q0;
            Q0=qCreatedBy(id+"F18.planeOp",FACE);
            var sketch = newSketch(context, id + "F21", { "sketchPlane" : qUnion([Q0])});
            skCircle(sketch, "E136", {"center": v(60, 0) * mm, "radius": 9 * mm});
            skSolve(sketch);
        }
        {
            var Q0;
            Q0=makeQuery(id+"F21.imprint","IMPRINT",FACE,{"disambiguationData":[TD([[makeQuery(id+"F21.imprint","IMPRINT",EDGE,{"derivedFrom":sQuery(id+"F21.wireOp",EDGE,"E136")}),1.0]])]});
            extrude(context, id + "F22", {"entities" : qUnion([Q0]), "endBound" : BoundingType.SYMMETRIC, "oppositeDirection" : true, "depth" : 11 * mm});
        }
        {
            var Q0;
            Q0=qCreatedBy(id+"F18.planeOp",FACE);
            cPlane(context, id + "F23", {"entities" : qUnion([Q0]), "cplaneType" : CPlaneType.OFFSET, "offset" : 7 * mm, "width" : 150 * mm, "height" : 150 * mm});
        }
        {
            var Q0;
            Q0=qCreatedBy(id+"F23.planeOp",FACE);
            var sketch = newSketch(context, id + "F24", { "sketchPlane" : qUnion([Q0])});
            skLineSegment(sketch, "E137", {"start": v(54.3, 7.63) * mm, "end": v(60.88, 8.56) * mm});
            skLineSegment(sketch, "E138", {"start": v(0, 0) * mm, "end": v(-61.2, 0) * mm});
            skArc(sketch, "E139", {"start": v(70, -0.72) * mm, "mid": v(70, 0) * mm, "end": v(70, 0.72) * mm});
            skLineSegment(sketch, "E140.MirrorCS", {"start": v(54.3, -7.63) * mm, "end": v(60.88, -8.56) * mm});
            skLineSegment(sketch, "E141", {"start": v(50, 2.68) * mm, "end": v(50, -2.68) * mm});
            skPoint(sketch, "E142.visualSharp", {"position": v(50, 7.03) * mm});
            skArc(sketch, "E142.filletArc", {"start": v(54.3, 7.63) * mm, "mid": v(51.23, 5.96) * mm, "end": v(50, 2.68) * mm});
            skPoint(sketch, "E143.visualSharp", {"position": v(50, -7.03) * mm});
            skArc(sketch, "E143.filletArc", {"start": v(50, -2.68) * mm, "mid": v(51.23, -5.96) * mm, "end": v(54.3, -7.63) * mm});
            skPoint(sketch, "E144.visualSharp", {"position": v(69.32, -9.74) * mm});
            skArc(sketch, "E144.filletArc", {"start": v(60.88, -8.56) * mm, "mid": v(67.21, -6.7) * mm, "end": v(70, -0.72) * mm});
            skPoint(sketch, "E145.visualSharp", {"position": v(69.32, 9.74) * mm});
            skArc(sketch, "E145.filletArc", {"start": v(70, 0.72) * mm, "mid": v(67.21, 6.7) * mm, "end": v(60.88, 8.56) * mm});
            skLineSegment(sketch, "E146.0", {"start": v(53.89, 10.6) * mm, "end": v(60.47, 11.53) * mm});
            skArc(sketch, "E147.0", {"start": v(73, 0.75) * mm, "mid": v(69.17, 8.97) * mm, "end": v(60.47, 11.53) * mm});
            skArc(sketch, "E147.1", {"start": v(73, -0.75) * mm, "mid": v(73, 0) * mm, "end": v(73, 0.75) * mm});
            skArc(sketch, "E147.2", {"start": v(60.47, -11.53) * mm, "mid": v(69.17, -8.97) * mm, "end": v(73, -0.75) * mm});
            skArc(sketch, "E147.3", {"start": v(53.89, 10.6) * mm, "mid": v(48.96, 7.93) * mm, "end": v(47, 2.68) * mm});
            skLineSegment(sketch, "E147.4", {"start": v(47, 2.68) * mm, "end": v(47, -2.68) * mm});
            skArc(sketch, "E147.5", {"start": v(47, -2.68) * mm, "mid": v(48.96, -7.93) * mm, "end": v(53.89, -10.6) * mm});
            skLineSegment(sketch, "E147.6", {"start": v(53.89, -10.6) * mm, "end": v(60.47, -11.53) * mm});
            skSolve(sketch);
        }
        {
            var Q0;
            Q0=makeQuery(id+"F24.imprint","IMPRINT",FACE,{"disambiguationData":[TD([[makeQuery(id+"F24.imprint","IMPRINT",EDGE,{"derivedFrom":sQuery(id+"F24.wireOp",EDGE,"E137")}),1.0]])]});
            extrude(context, id + "F25", {"entities" : qUnion([Q0]), "depth" : 4 * mm});
        }
        {
            var Q0;
            Q0=makeQuery(id+"F25.opExtrude","SWEPT_BODY",BODY,{"disambiguationData":[OSD([sQuery(id+"F24.wireOp",EDGE,"E137"),sQuery(id+"F24.wireOp",EDGE,"E139"),sQuery(id+"F24.wireOp",EDGE,"E140.MirrorCS"),sQuery(id+"F24.wireOp",EDGE,"E141"),sQuery(id+"F24.wireOp",EDGE,"E142.filletArc"),sQuery(id+"F24.wireOp",EDGE,"E143.filletArc"),sQuery(id+"F24.wireOp",EDGE,"E144.filletArc"),sQuery(id+"F24.wireOp",EDGE,"E145.filletArc"),sQuery(id+"F24.wireOp",EDGE,"E146.0"),sQuery(id+"F24.wireOp",EDGE,"E147.0"),sQuery(id+"F24.wireOp",EDGE,"E147.1"),sQuery(id+"F24.wireOp",EDGE,"E147.2"),sQuery(id+"F24.wireOp",EDGE,"E147.3"),sQuery(id+"F24.wireOp",EDGE,"E147.4"),sQuery(id+"F24.wireOp",EDGE,"E147.5"),sQuery(id+"F24.wireOp",EDGE,"E147.6")])]});
            var Q1;
            Q1=qCreatedBy(id+"F18.planeOp",FACE);
            mirror(context, id + "F26", {"entities" : qUnion([Q0]), "mirrorPlane" : qUnion([Q1])});
        }
        {
            var Q0;
            Q0=makeQuery(id+"F25.opExtrude","SWEPT_BODY",BODY,{"disambiguationData":[OSD([sQuery(id+"F24.wireOp",EDGE,"E137"),sQuery(id+"F24.wireOp",EDGE,"E139"),sQuery(id+"F24.wireOp",EDGE,"E140.MirrorCS"),sQuery(id+"F24.wireOp",EDGE,"E141"),sQuery(id+"F24.wireOp",EDGE,"E142.filletArc"),sQuery(id+"F24.wireOp",EDGE,"E143.filletArc"),sQuery(id+"F24.wireOp",EDGE,"E144.filletArc"),sQuery(id+"F24.wireOp",EDGE,"E145.filletArc"),sQuery(id+"F24.wireOp",EDGE,"E146.0"),sQuery(id+"F24.wireOp",EDGE,"E147.0"),sQuery(id+"F24.wireOp",EDGE,"E147.1"),sQuery(id+"F24.wireOp",EDGE,"E147.2"),sQuery(id+"F24.wireOp",EDGE,"E147.3"),sQuery(id+"F24.wireOp",EDGE,"E147.4"),sQuery(id+"F24.wireOp",EDGE,"E147.5"),sQuery(id+"F24.wireOp",EDGE,"E147.6")])]});
            var Q1;
            Q1=makeQuery(id+"F26.opPattern","COPY",BODY,{"derivedFrom":makeQuery(id+"F25.opExtrude","SWEPT_BODY",BODY,{"disambiguationData":[OSD([sQuery(id+"F24.wireOp",EDGE,"E137"),sQuery(id+"F24.wireOp",EDGE,"E139"),sQuery(id+"F24.wireOp",EDGE,"E140.MirrorCS"),sQuery(id+"F24.wireOp",EDGE,"E141"),sQuery(id+"F24.wireOp",EDGE,"E142.filletArc"),sQuery(id+"F24.wireOp",EDGE,"E143.filletArc"),sQuery(id+"F24.wireOp",EDGE,"E144.filletArc"),sQuery(id+"F24.wireOp",EDGE,"E145.filletArc"),sQuery(id+"F24.wireOp",EDGE,"E146.0"),sQuery(id+"F24.wireOp",EDGE,"E147.0"),sQuery(id+"F24.wireOp",EDGE,"E147.1"),sQuery(id+"F24.wireOp",EDGE,"E147.2"),sQuery(id+"F24.wireOp",EDGE,"E147.3"),sQuery(id+"F24.wireOp",EDGE,"E147.4"),sQuery(id+"F24.wireOp",EDGE,"E147.5"),sQuery(id+"F24.wireOp",EDGE,"E147.6")])]}),"instanceName":"1"});
            var Q2;
            Q2=makeQuery(id+"F22.opExtrude","SWEPT_BODY",BODY,{"disambiguationData":[OSD([sQuery(id+"F21.wireOp",EDGE,"E136")])]});
            var Q3;
            Q3=sQuery(id+"F1.wireOp",EDGE,"E33");
            circularPattern(context, id + "F27", {"entities" : qUnion([Q0, Q1, Q2]), "axis" : qUnion([Q3]), "angle" : 360 * degree, "instanceCount" : round(12), "equalSpace" : true});
        }
        {
            var Q0;
            Q0=makeQuery(id+"F22.opExtrude","SWEPT_BODY",BODY,{"disambiguationData":[OSD([sQuery(id+"F21.wireOp",EDGE,"E136")])]});
            var Q1;
            Q1=makeQuery(id+"F27.opPattern","COPY",BODY,{"derivedFrom":makeQuery(id+"F22.opExtrude","SWEPT_BODY",BODY,{"disambiguationData":[OSD([sQuery(id+"F21.wireOp",EDGE,"E136")])]}),"instanceName":"11"});
            var Q2;
            Q2=makeQuery(id+"F27.opPattern","COPY",BODY,{"derivedFrom":makeQuery(id+"F22.opExtrude","SWEPT_BODY",BODY,{"disambiguationData":[OSD([sQuery(id+"F21.wireOp",EDGE,"E136")])]}),"instanceName":"10"});
            var Q3;
            Q3=makeQuery(id+"F27.opPattern","COPY",BODY,{"derivedFrom":makeQuery(id+"F22.opExtrude","SWEPT_BODY",BODY,{"disambiguationData":[OSD([sQuery(id+"F21.wireOp",EDGE,"E136")])]}),"instanceName":"9"});
            var Q4;
            Q4=makeQuery(id+"F27.opPattern","COPY",BODY,{"derivedFrom":makeQuery(id+"F22.opExtrude","SWEPT_BODY",BODY,{"disambiguationData":[OSD([sQuery(id+"F21.wireOp",EDGE,"E136")])]}),"instanceName":"8"});
            var Q5;
            Q5=makeQuery(id+"F27.opPattern","COPY",BODY,{"derivedFrom":makeQuery(id+"F22.opExtrude","SWEPT_BODY",BODY,{"disambiguationData":[OSD([sQuery(id+"F21.wireOp",EDGE,"E136")])]}),"instanceName":"7"});
            var Q6;
            Q6=makeQuery(id+"F27.opPattern","COPY",BODY,{"derivedFrom":makeQuery(id+"F22.opExtrude","SWEPT_BODY",BODY,{"disambiguationData":[OSD([sQuery(id+"F21.wireOp",EDGE,"E136")])]}),"instanceName":"6"});
            var Q7;
            Q7=makeQuery(id+"F27.opPattern","COPY",BODY,{"derivedFrom":makeQuery(id+"F22.opExtrude","SWEPT_BODY",BODY,{"disambiguationData":[OSD([sQuery(id+"F21.wireOp",EDGE,"E136")])]}),"instanceName":"5"});
            var Q8;
            Q8=makeQuery(id+"F27.opPattern","COPY",BODY,{"derivedFrom":makeQuery(id+"F22.opExtrude","SWEPT_BODY",BODY,{"disambiguationData":[OSD([sQuery(id+"F21.wireOp",EDGE,"E136")])]}),"instanceName":"4"});
            var Q9;
            Q9=makeQuery(id+"F27.opPattern","COPY",BODY,{"derivedFrom":makeQuery(id+"F22.opExtrude","SWEPT_BODY",BODY,{"disambiguationData":[OSD([sQuery(id+"F21.wireOp",EDGE,"E136")])]}),"instanceName":"3"});
            var Q10;
            Q10=makeQuery(id+"F27.opPattern","COPY",BODY,{"derivedFrom":makeQuery(id+"F22.opExtrude","SWEPT_BODY",BODY,{"disambiguationData":[OSD([sQuery(id+"F21.wireOp",EDGE,"E136")])]}),"instanceName":"2"});
            var Q11;
            Q11=makeQuery(id+"F27.opPattern","COPY",BODY,{"derivedFrom":makeQuery(id+"F22.opExtrude","SWEPT_BODY",BODY,{"disambiguationData":[OSD([sQuery(id+"F21.wireOp",EDGE,"E136")])]}),"instanceName":"1"});
            var Q12;
            Q12=makeQuery(id+"F20.opExtrude","SWEPT_BODY",BODY,{"disambiguationData":[OSD([sQuery(id+"F19.wireOp",EDGE,"E134"),sQuery(id+"F19.wireOp",EDGE,"E135")])]});
            booleanBodies(context, id + "F28", {"operationType" : BooleanOperationType.SUBTRACTION, "tools" : qUnion([Q0, Q1, Q2, Q3, Q4, Q5, Q6, Q7, Q8, Q9, Q10, Q11]), "targets" : qUnion([Q12]), "keepTools" : true});
        }
        {
            var Q0;
            Q0=makeQuery(id+"F0.imprint","IMPRINT",FACE,{"disambiguationData":[TD([[makeQuery(id+"F0.imprint","IMPRINT",EDGE,{"derivedFrom":sQuery(id+"F0.wireOp",EDGE,"E3")}),1.0]])]});
            extrude(context, id + "F29", {"entities" : qUnion([Q0]), "depth" : 220 * mm, "hasSecondDirection" : true, "secondDirectionOppositeDirection" : true, "secondDirectionDepth" : 50 * mm});
        }
        {
            var Q0;
            Q0=qCreatedBy(makeId("Right.planeOp"),FACE);
            var sketch = newSketch(context, id + "F30", { "sketchPlane" : qUnion([Q0])});
            skLineSegment(sketch, "E148", {"start": v(0, 0) * mm, "end": v(0, -60.19) * mm, "construction": true});
            skLineSegment(sketch, "E149", {"start": v(0, 0) * mm, "end": v(-41.84, 0) * mm, "construction": true});
            skCircle(sketch, "E150", {"center": v(42, 0) * mm, "radius": 18 * mm});
            skLineSegment(sketch, "E151", {"start": v(42, 0) * mm, "end": v(60, 0) * mm});
            skLineSegment(sketch, "E152", {"start": v(0, 18) * mm, "end": v(0, 0) * mm});
            skLineSegment(sketch, "E153", {"start": v(0, 18) * mm, "end": v(42, 18) * mm});
            skLineSegment(sketch, "E154", {"start": v(0, -7) * mm, "end": v(25.42, -7) * mm});
            skLineSegment(sketch, "E155", {"start": v(13, 18) * mm, "end": v(13, -7) * mm});
            skLineSegment(sketch, "E156", {"start": v(0, 0) * mm, "end": v(0, -7) * mm});
            skLineSegment(sketch, "E157", {"start": v(0, 18) * mm, "end": v(0, 27.9) * mm});
            skLineSegment(sketch, "E158", {"start": v(0, 27.9) * mm, "end": v(71, 27.9) * mm});
            skLineSegment(sketch, "E159", {"start": v(71, 27.9) * mm, "end": v(71, -33.15) * mm});
            skLineSegment(sketch, "E160", {"start": v(71, -33.15) * mm, "end": v(0, -33.15) * mm});
            skPoint(sketch, "E160.endSnap0", {"position": v(0, -30.1) * mm});
            skLineSegment(sketch, "E161", {"start": v(0, -33.15) * mm, "end": v(0, -7) * mm});
            skLineSegment(sketch, "E162", {"start": v(60, 0) * mm, "end": v(71, 0) * mm});
            skPoint(sketch, "E162.endSnap0", {"position": v(71, -2.62) * mm});
            skSolve(sketch);
        }
        {
            var Q0;
            {var subQ0=sQuery(id+"F30.wireOp",EDGE,"E157");Q0=makeQuery(id+"F30.imprint","IMPRINT",FACE,{"disambiguationData":[TD([[makeQuery(id+"F30.imprint","IMPRINT",EDGE,{"derivedFrom":subQ0}),-1.0]])]});}
            var Q1;
            Q1=sQuery(id+"F30.wireOp",EDGE,"E148");
            revolve(context, id + "F31", {"entities" : qUnion([Q0]), "axis" : qUnion([Q1]), "revolveType" : RevolveType.FULL});
        }
        {
            var Q0;
            {var subQ0=sQuery(id+"F30.wireOp",EDGE,"E160");Q0=makeQuery(id+"F30.imprint","IMPRINT",FACE,{"disambiguationData":[TD([[makeQuery(id+"F30.imprint","IMPRINT",EDGE,{"derivedFrom":subQ0}),-1.0]])]});}
            var Q1;
            Q1=sQuery(id+"F30.wireOp",EDGE,"E148");
            revolve(context, id + "F32", {"entities" : qUnion([Q0]), "axis" : qUnion([Q1]), "revolveType" : RevolveType.FULL});
        }
        {
            var Q0;
            {var subQ0=sQuery(id+"F30.wireOp",EDGE,"E150");var subQ1=makeQuery(id+"F30.imprint","INTERSECT",VERTEX,{"derivedFrom":[subQ0,sQuery(id+"F30.wireOp",EDGE,"E162")]});Q0=makeQuery(id+"F30.imprint","IMPRINT",FACE,{"disambiguationData":[TD([[makeQuery(id+"F30.imprint","IMPRINT",EDGE,{"disambiguationData":[TD([[subQ1,-1.0]])],"derivedFrom":subQ0}),1.0]])]});}
            var Q1;
            {var subQ5=sQuery(id+"F30.wireOp",EDGE,"E155");Q1=makeQuery(id+"F30.imprint","IMPRINT",FACE,{"disambiguationData":[TD([[makeQuery(id+"F30.imprint","IMPRINT",EDGE,{"derivedFrom":subQ5}),1.0]])]});}
            var Q2;
            Q2=makeQuery(id+"F31.opRevolve","SWEPT_FACE",FACE,{"disambiguationData":[OSD([sQuery(id+"F30.wireOp",EDGE,"E159")])]});
            revolve(context, id + "F33", {"entities" : qUnion([Q0, Q1]), "axis" : qUnion([Q2]), "revolveType" : RevolveType.SYMMETRIC, "angle" : 50 * degree});
        }
        {
            var Q0;
            Q0=makeQuery(id+"F33.opRevolve","SWEPT_BODY",BODY,{"disambiguationData":[OSD([sQuery(id+"F30.wireOp",EDGE,"E150"),sQuery(id+"F30.wireOp",EDGE,"E153"),sQuery(id+"F30.wireOp",EDGE,"E154"),sQuery(id+"F30.wireOp",EDGE,"E155")])]});
            var Q1;
            Q1=sQuery(id+"F30.wireOp",EDGE,"E148");
            circularPattern(context, id + "F34", {"entities" : qUnion([Q0]), "axis" : qUnion([Q1]), "angle" : 180 * degree, "instanceCount" : 2});
        }
        {
            var Q0;
            {var subQ0=sQuery(id+"F30.wireOp",EDGE,"E150");var subQ1=makeQuery(id+"F30.imprint","INTERSECT",VERTEX,{"derivedFrom":[subQ0,sQuery(id+"F30.wireOp",EDGE,"E162")]});Q0=makeQuery(id+"F30.imprint","IMPRINT",FACE,{"disambiguationData":[TD([[makeQuery(id+"F30.imprint","IMPRINT",EDGE,{"disambiguationData":[TD([[subQ1,-1.0]])],"derivedFrom":subQ0}),1.0]])]});}
            var Q1;
            {var subQ5=sQuery(id+"F30.wireOp",EDGE,"E155");Q1=makeQuery(id+"F30.imprint","IMPRINT",FACE,{"disambiguationData":[TD([[makeQuery(id+"F30.imprint","IMPRINT",EDGE,{"derivedFrom":subQ5}),1.0]])]});}
            var Q2;
            Q2=sQuery(id+"F30.wireOp",EDGE,"E148");
            revolve(context, id + "F35", {"entities" : qUnion([Q0, Q1]), "axis" : qUnion([Q2]), "revolveType" : RevolveType.SYMMETRIC, "angle" : 40 * degree});
        }
        {
            var Q0;
            Q0=makeQuery(id+"F35.opRevolve","SWEPT_BODY",BODY,{"disambiguationData":[OSD([sQuery(id+"F30.wireOp",EDGE,"E150"),sQuery(id+"F30.wireOp",EDGE,"E153"),sQuery(id+"F30.wireOp",EDGE,"E154"),sQuery(id+"F30.wireOp",EDGE,"E155")])]});
            var Q1;
            Q1=sQuery(id+"F30.wireOp",EDGE,"E148");
            circularPattern(context, id + "F36", {"entities" : qUnion([Q0]), "axis" : qUnion([Q1]), "angle" : 180 * degree, "instanceCount" : 2});
        }
        {
            var Q0;
            {var subQ2=sQuery(id+"F30.wireOp",EDGE,"E152");Q0=makeQuery(id+"F30.imprint","IMPRINT",FACE,{"disambiguationData":[TD([[makeQuery(id+"F30.imprint","IMPRINT",EDGE,{"derivedFrom":subQ2}),1.0]])]});}
            var Q1;
            Q1=sQuery(id+"F30.wireOp",EDGE,"E148");
            revolve(context, id + "F37", {"entities" : qUnion([Q0]), "axis" : qUnion([Q1]), "revolveType" : RevolveType.FULL});
        }
        {
            var Q0;
            {var subQ5=sQuery(id+"F30.wireOp",EDGE,"E155");Q0=makeQuery(id+"F30.imprint","IMPRINT",FACE,{"disambiguationData":[TD([[makeQuery(id+"F30.imprint","IMPRINT",EDGE,{"derivedFrom":subQ5}),1.0]])]});}
            var Q1;
            {var subQ0=sQuery(id+"F30.wireOp",EDGE,"E150");var subQ1=makeQuery(id+"F30.imprint","INTERSECT",VERTEX,{"derivedFrom":[subQ0,sQuery(id+"F30.wireOp",EDGE,"E162")]});Q1=makeQuery(id+"F30.imprint","IMPRINT",FACE,{"disambiguationData":[TD([[makeQuery(id+"F30.imprint","IMPRINT",EDGE,{"disambiguationData":[TD([[subQ1,-1.0]])],"derivedFrom":subQ0}),1.0]])]});}
            var Q2;
            Q2=sQuery(id+"F30.wireOp",EDGE,"E148");
            revolve(context, id + "F38", {"entities" : qUnion([Q0, Q1]), "axis" : qUnion([Q2]), "revolveType" : RevolveType.SYMMETRIC, "angle" : 90 * degree});
        }
        {
            var Q0;
            {var subQ1=sQuery(id+"F1.wireOp",EDGE,"E31.rect.bottom");Q0=makeQuery(id+"F1.imprint","IMPRINT",FACE,{"disambiguationData":[TD([[makeQuery(id+"F1.imprint","IMPRINT",EDGE,{"derivedFrom":subQ1}),-1.0]])]});}
            var Q1;
            {var subQ0=sQuery(id+"F1.wireOp",EDGE,"E31.rect.top");Q1=makeQuery(id+"F1.imprint","IMPRINT",FACE,{"disambiguationData":[TD([[makeQuery(id+"F1.imprint","IMPRINT",EDGE,{"derivedFrom":subQ0}),1.0]])]});}
            var Q2;
            Q2=sQuery(id+"F1.wireOp",EDGE,"E33");
            revolve(context, id + "F39", {"entities" : qUnion([Q0, Q1]), "axis" : qUnion([Q2]), "revolveType" : RevolveType.FULL});
        }
    });
